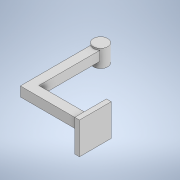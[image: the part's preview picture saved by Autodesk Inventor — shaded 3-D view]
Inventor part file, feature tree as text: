
AUTODESK INVENTOR PART (.ipt)
format: ipt  version: 2020.2 (Build 242310000, 310)  size: 172,032 bytes
history: native  units: in
note: dims shown in document units (in); Inventor stores cm internally (conversion verified against a paired STEP export)
features: extrude x6, sketch x6, projected_geometry x2
ambient origin geometry x8: Origin, YZ Plane, XZ Plane, XY Plane, X Axis, Y Axis, Z Axis, Center Point
bodies: Body1 (feature_tree)
feature tree (14):
  extrude  "Extrusion2"  Depth=0.2047in
  extrude  "Extrusion3"  Depth=0.0394in
  extrude  "Extrusion4"  Depth=0.0394in TaperAngle=0.0deg
  extrude  "Extrusion7"  Depth=0.1181in
  extrude  "Extrusion8"  Depth=0.1181in
  extrude  "Extrusion11"  Depth=0.2362in
  sketch  "Sketch3"  dims[d10=0.3543in d11=0.2047in]
  sketch  "Sketch4"  dims[d12=0.1575in d13=0.0in d14=0.0394in]
  projected_geometry  "Projected Loop1"
  sketch  "Sketch5"  dims[d16=0.2362in d17=0.0in d18=0.0394in d19=0.0in]
  sketch  "Sketch6"  dims[d20=0.0394in d21=0.1181in]
  sketch  "Sketch8"  dims[d22=90.0deg d32=0.1181in]
  projected_geometry  "Projected Loop2"
  sketch  "Sketch11"  dims[d33=180.0deg d34=0.2362in d35=90.0deg d36=0.2362in d37=90.0deg d38=1.8189in d39=0.0in d40=0.2362in d41=1.4in d42=0.0in d59=0.2755in d60=0.276in d61=0.787in d62=0.787in d63=0.1181in d64=0.0in]
